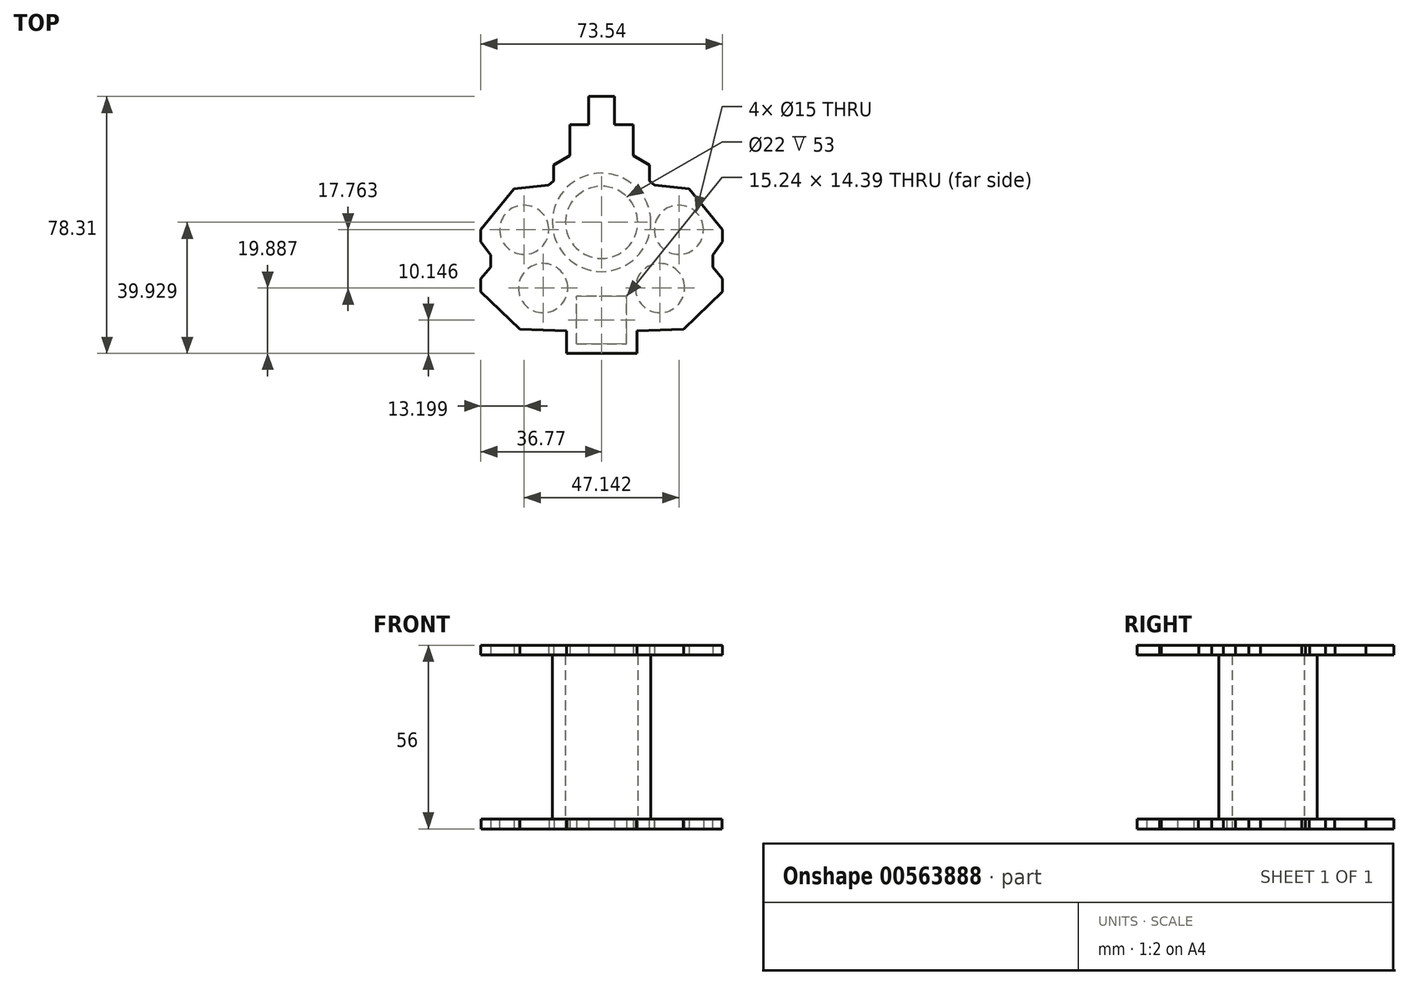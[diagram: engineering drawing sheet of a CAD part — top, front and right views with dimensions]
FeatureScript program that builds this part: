
annotation { "Feature Type Name" : "Feature", "Feature Type Description" : "" }
export const myFeature = defineFeature(function(context is Context, id is Id, definition is map)
    precondition{}
    {
        {
            var Q0;
            Q0=qCreatedBy(makeId("Top.planeOp"),FACE);
            var sketch = newSketch(context, id + "F0", { "sketchPlane" : qUnion([Q0])});
            skCircle(sketch, "E0", {"center": v(23.57, 0) * mm, "radius": 7.5 * mm});
            skCircle(sketch, "E1", {"center": v(17.81, -17.76) * mm, "radius": 7.5 * mm});
            skArc(sketch, "E2", {"start": v(0, -8.72) * mm, "mid": v(11, 2.28) * mm, "end": v(0, 13.28) * mm});
            skLineSegment(sketch, "E3", {"start": v(0, 40.64) * mm, "end": v(3.87, 40.64) * mm});
            skLineSegment(sketch, "E4", {"start": v(3.87, 40.64) * mm, "end": v(3.87, 32.06) * mm});
            skLineSegment(sketch, "E5", {"start": v(3.87, 32.06) * mm, "end": v(9.65, 32.06) * mm});
            skLineSegment(sketch, "E6", {"start": v(9.65, 32.06) * mm, "end": v(9.65, 22.64) * mm});
            skLineSegment(sketch, "E7", {"start": v(9.65, 22.64) * mm, "end": v(14.5, 19.75) * mm});
            skLineSegment(sketch, "E8", {"start": v(14.5, 19.75) * mm, "end": v(14.5, 14.89) * mm});
            skLineSegment(sketch, "E9", {"start": v(14.5, 14.89) * mm, "end": v(16.03, 13.67) * mm});
            skLineSegment(sketch, "E10", {"start": v(16.03, 13.67) * mm, "end": v(26.65, 12.48) * mm});
            skLineSegment(sketch, "E11", {"start": v(26.65, 12.48) * mm, "end": v(36.72, 0) * mm});
            skLineSegment(sketch, "E12", {"start": v(36.72, 0) * mm, "end": v(36.72, -3.62) * mm});
            skLineSegment(sketch, "E13", {"start": v(36.72, -3.62) * mm, "end": v(33.8, -7.65) * mm});
            skLineSegment(sketch, "E14", {"start": v(33.8, -7.65) * mm, "end": v(33.8, -11.37) * mm});
            skLineSegment(sketch, "E15", {"start": v(33.8, -11.37) * mm, "end": v(36.72, -14.9) * mm});
            skLineSegment(sketch, "E16", {"start": v(36.72, -14.9) * mm, "end": v(36.72, -18.9) * mm});
            skLineSegment(sketch, "E17", {"start": v(36.72, -18.9) * mm, "end": v(24.9, -30.27) * mm});
            skLineSegment(sketch, "E18", {"start": v(24.9, -30.27) * mm, "end": v(10.68, -30.78) * mm});
            skLineSegment(sketch, "E19", {"start": v(10.68, -30.78) * mm, "end": v(10.68, -37.65) * mm});
            skLineSegment(sketch, "E20", {"start": v(10.68, -37.65) * mm, "end": v(0, -37.65) * mm});
            skLineSegment(sketch, "E21", {"start": v(0, 40.64) * mm, "end": v(0, 13.28) * mm});
            skLineSegment(sketch, "E22", {"start": v(0, -37.65) * mm, "end": v(0, -34.7) * mm});
            skLineSegment(sketch, "E23", {"start": v(0, -34.7) * mm, "end": v(7.62, -34.7) * mm});
            skLineSegment(sketch, "E24", {"start": v(7.62, -34.7) * mm, "end": v(7.62, -20.31) * mm});
            skLineSegment(sketch, "E25", {"start": v(7.62, -20.31) * mm, "end": v(0, -20.31) * mm});
            skLineSegment(sketch, "E26", {"start": v(0, -20.31) * mm, "end": v(0, -8.72) * mm});
            skSolve(sketch);
        }
        {
            var Q0;
            Q0 = qSketchRegion(id + "F0", true);
            extrude(context, id + "F1", {"entities" : qUnion([Q0]), "depth" : 3 * mm, "offsetDistance" : 25 * mm});
        }
        {
            var Q0;
            Q0=makeQuery(id+"F1.opExtrude","SWEPT_BODY",BODY,{"disambiguationData":[OSD([sQuery(id+"F0.wireOp",EDGE,"E0"),sQuery(id+"F0.wireOp",EDGE,"E1"),sQuery(id+"F0.wireOp",EDGE,"E2"),sQuery(id+"F0.wireOp",EDGE,"E3"),sQuery(id+"F0.wireOp",EDGE,"E4"),sQuery(id+"F0.wireOp",EDGE,"E5"),sQuery(id+"F0.wireOp",EDGE,"E6"),sQuery(id+"F0.wireOp",EDGE,"E7"),sQuery(id+"F0.wireOp",EDGE,"E8"),sQuery(id+"F0.wireOp",EDGE,"E9"),sQuery(id+"F0.wireOp",EDGE,"E10"),sQuery(id+"F0.wireOp",EDGE,"E11"),sQuery(id+"F0.wireOp",EDGE,"E12"),sQuery(id+"F0.wireOp",EDGE,"E13"),sQuery(id+"F0.wireOp",EDGE,"E14"),sQuery(id+"F0.wireOp",EDGE,"E15"),sQuery(id+"F0.wireOp",EDGE,"E16"),sQuery(id+"F0.wireOp",EDGE,"E17"),sQuery(id+"F0.wireOp",EDGE,"E18"),sQuery(id+"F0.wireOp",EDGE,"E19"),sQuery(id+"F0.wireOp",EDGE,"E20"),sQuery(id+"F0.wireOp",EDGE,"E21"),sQuery(id+"F0.wireOp",EDGE,"E22"),sQuery(id+"F0.wireOp",EDGE,"E23"),sQuery(id+"F0.wireOp",EDGE,"E24"),sQuery(id+"F0.wireOp",EDGE,"E25"),sQuery(id+"F0.wireOp",EDGE,"E26")])]});
            var Q1;
            Q1=qCreatedBy(makeId("Right.planeOp"),FACE);
            mirror(context, id + "F2", {"operationType" : NewBodyOperationType.ADD, "entities" : qUnion([Q0]), "mirrorPlane" : qUnion([Q1])});
        }
        {
            var Q0;
            {var subQ0=makeQuery(id+"F1.opExtrude","CAP_FACE",FACE,{"disambiguationData":[OSD([sQuery(id+"F0.wireOp",EDGE,"E0"),sQuery(id+"F0.wireOp",EDGE,"E1"),sQuery(id+"F0.wireOp",EDGE,"E2"),sQuery(id+"F0.wireOp",EDGE,"E3"),sQuery(id+"F0.wireOp",EDGE,"E4"),sQuery(id+"F0.wireOp",EDGE,"E5"),sQuery(id+"F0.wireOp",EDGE,"E6"),sQuery(id+"F0.wireOp",EDGE,"E7"),sQuery(id+"F0.wireOp",EDGE,"E8"),sQuery(id+"F0.wireOp",EDGE,"E9"),sQuery(id+"F0.wireOp",EDGE,"E10"),sQuery(id+"F0.wireOp",EDGE,"E11"),sQuery(id+"F0.wireOp",EDGE,"E12"),sQuery(id+"F0.wireOp",EDGE,"E13"),sQuery(id+"F0.wireOp",EDGE,"E14"),sQuery(id+"F0.wireOp",EDGE,"E15"),sQuery(id+"F0.wireOp",EDGE,"E16"),sQuery(id+"F0.wireOp",EDGE,"E17"),sQuery(id+"F0.wireOp",EDGE,"E18"),sQuery(id+"F0.wireOp",EDGE,"E19"),sQuery(id+"F0.wireOp",EDGE,"E20"),sQuery(id+"F0.wireOp",EDGE,"E21"),sQuery(id+"F0.wireOp",EDGE,"E22"),sQuery(id+"F0.wireOp",EDGE,"E23"),sQuery(id+"F0.wireOp",EDGE,"E24"),sQuery(id+"F0.wireOp",EDGE,"E25"),sQuery(id+"F0.wireOp",EDGE,"E26")])],"isStart":false});Q0=makeQuery(id+"F2.boolean.opBoolean","MERGE",FACE,{"derivedFrom":[subQ0,makeQuery(id+"F2.opPattern","COPY",FACE,{"derivedFrom":subQ0,"instanceName":"1"})]});}
            var sketch = newSketch(context, id + "F3", { "sketchPlane" : qUnion([Q0])});
            skCircle(sketch, "E27", {"center": v(0, 2.28) * mm, "radius": 11 * mm});
            skCircle(sketch, "E28", {"center": v(0, 2.28) * mm, "radius": 15 * mm});
            skSolve(sketch);
        }
        {
            var Q0;
            Q0 = qSketchRegion(id + "F3", true);
            extrude(context, id + "F4", {"entities" : qUnion([Q0]), "operationType" : NewBodyOperationType.ADD, "depth" : 50 * mm, "offsetDistance" : 25 * mm});
        }
        {
            var Q0;
            Q0=makeQuery(id+"F4.opExtrude","CAP_FACE",FACE,{"disambiguationData":[OSD([sQuery(id+"F3.wireOp",EDGE,"E27"),sQuery(id+"F3.wireOp",EDGE,"E28")])],"isStart":false});
            var sketch = newSketch(context, id + "F5", { "sketchPlane" : qUnion([Q0])});
            skLineSegment(sketch, "E29", {"start": v(0, 40.66) * mm, "end": v(3.87, 40.66) * mm});
            skLineSegment(sketch, "E30", {"start": v(3.87, 40.66) * mm, "end": v(3.87, 32.07) * mm});
            skLineSegment(sketch, "E31", {"start": v(3.87, 32.07) * mm, "end": v(9.7, 32.07) * mm});
            skLineSegment(sketch, "E32", {"start": v(9.7, 32.07) * mm, "end": v(9.7, 22.65) * mm});
            skLineSegment(sketch, "E33", {"start": v(9.7, 22.65) * mm, "end": v(14.56, 19.77) * mm});
            skLineSegment(sketch, "E34", {"start": v(14.56, 19.77) * mm, "end": v(14.56, 14.9) * mm});
            skLineSegment(sketch, "E35", {"start": v(14.56, 14.9) * mm, "end": v(16.08, 13.69) * mm});
            skLineSegment(sketch, "E36", {"start": v(16.08, 13.69) * mm, "end": v(26.7, 12.5) * mm});
            skLineSegment(sketch, "E37", {"start": v(26.7, 12.5) * mm, "end": v(36.77, 0.02) * mm});
            skLineSegment(sketch, "E38", {"start": v(36.77, 0.02) * mm, "end": v(36.77, -3.6) * mm});
            skLineSegment(sketch, "E39", {"start": v(36.77, -3.6) * mm, "end": v(33.85, -7.63) * mm});
            skLineSegment(sketch, "E40", {"start": v(33.85, -7.63) * mm, "end": v(33.85, -11.36) * mm});
            skLineSegment(sketch, "E41", {"start": v(33.85, -11.36) * mm, "end": v(36.77, -14.89) * mm});
            skLineSegment(sketch, "E42", {"start": v(36.77, -14.89) * mm, "end": v(36.77, -18.88) * mm});
            skLineSegment(sketch, "E43", {"start": v(36.77, -18.88) * mm, "end": v(24.96, -30.25) * mm});
            skLineSegment(sketch, "E44", {"start": v(24.96, -30.25) * mm, "end": v(10.73, -30.76) * mm});
            skLineSegment(sketch, "E45", {"start": v(10.73, -30.76) * mm, "end": v(10.73, -37.63) * mm});
            skLineSegment(sketch, "E46", {"start": v(10.73, -37.63) * mm, "end": v(0, -37.63) * mm});
            skLineSegment(sketch, "E47", {"start": v(0, -37.63) * mm, "end": v(0, 40.66) * mm});
            skSolve(sketch);
        }
        {
            var Q0;
            Q0 = qSketchRegion(id + "F5", true);
            extrude(context, id + "F6", {"entities" : qUnion([Q0]), "depth" : 3 * mm, "offsetDistance" : 25 * mm});
        }
        {
            var Q0;
            Q0=makeQuery(id+"F6.opExtrude","SWEPT_BODY",BODY,{"disambiguationData":[OSD([sQuery(id+"F5.wireOp",EDGE,"E29"),sQuery(id+"F5.wireOp",EDGE,"E30"),sQuery(id+"F5.wireOp",EDGE,"E31"),sQuery(id+"F5.wireOp",EDGE,"E32"),sQuery(id+"F5.wireOp",EDGE,"E33"),sQuery(id+"F5.wireOp",EDGE,"E34"),sQuery(id+"F5.wireOp",EDGE,"E35"),sQuery(id+"F5.wireOp",EDGE,"E36"),sQuery(id+"F5.wireOp",EDGE,"E37"),sQuery(id+"F5.wireOp",EDGE,"E38"),sQuery(id+"F5.wireOp",EDGE,"E39"),sQuery(id+"F5.wireOp",EDGE,"E40"),sQuery(id+"F5.wireOp",EDGE,"E41"),sQuery(id+"F5.wireOp",EDGE,"E42"),sQuery(id+"F5.wireOp",EDGE,"E43"),sQuery(id+"F5.wireOp",EDGE,"E44"),sQuery(id+"F5.wireOp",EDGE,"E45"),sQuery(id+"F5.wireOp",EDGE,"E46"),sQuery(id+"F5.wireOp",EDGE,"E47")])]});
            var Q1;
            Q1=qCreatedBy(makeId("Right.planeOp"),FACE);
            mirror(context, id + "F7", {"operationType" : NewBodyOperationType.ADD, "entities" : qUnion([Q0]), "mirrorPlane" : qUnion([Q1])});
        }
    });
